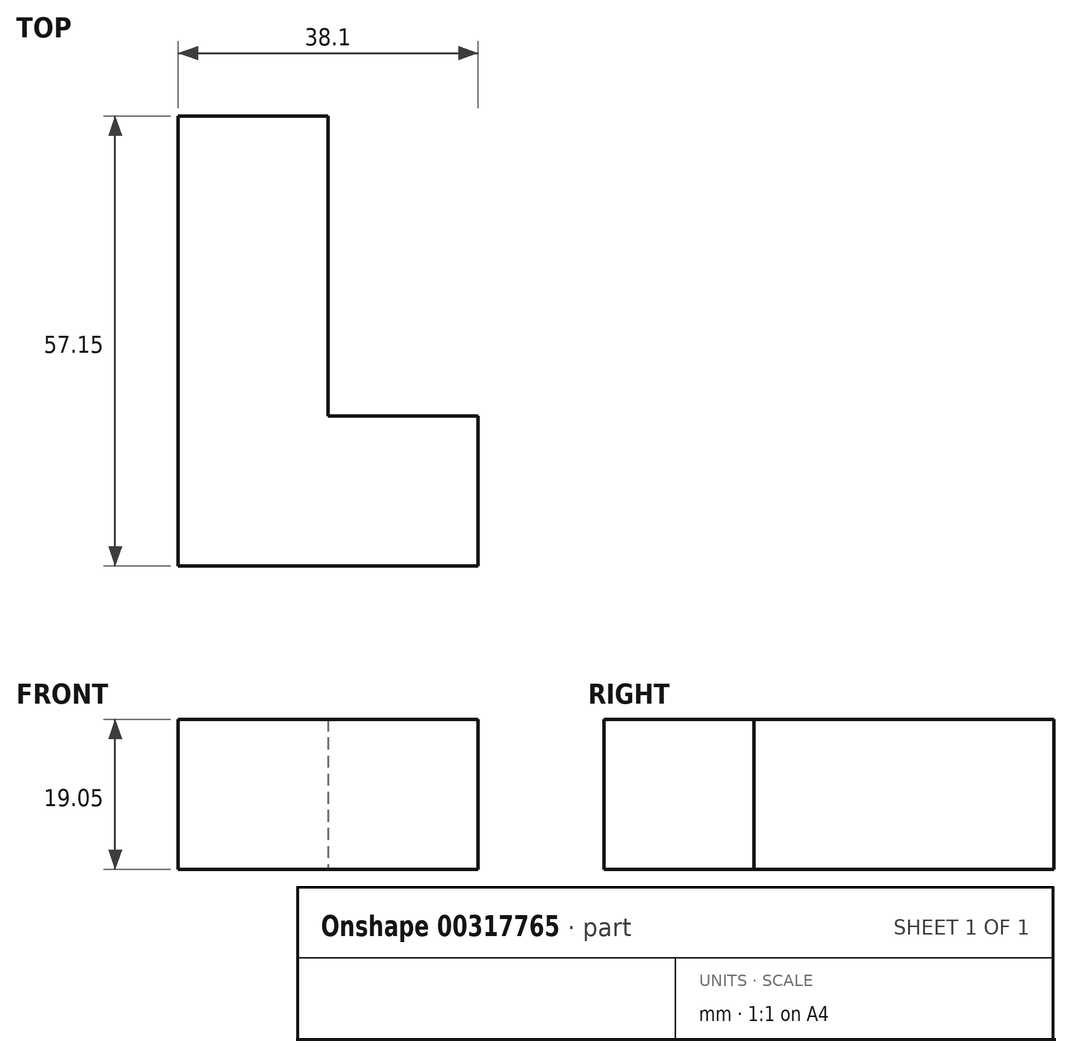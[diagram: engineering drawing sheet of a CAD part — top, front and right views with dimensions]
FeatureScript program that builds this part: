
annotation { "Feature Type Name" : "Feature", "Feature Type Description" : "" }
export const myFeature = defineFeature(function(context is Context, id is Id, definition is map)
    precondition{}
    {
        {
            var Q0;
            Q0=qCreatedBy(makeId("Top.planeOp"),FACE);
            var sketch = newSketch(context, id + "F0", { "sketchPlane" : qUnion([Q0])});
            skLineSegment(sketch, "E0.bottom", {"start": v(0, 0) * mm, "end": v(19.05, 0) * mm});
            skLineSegment(sketch, "E0.top", {"start": v(0, 57.15) * mm, "end": v(19.05, 57.15) * mm});
            skLineSegment(sketch, "E0.left", {"start": v(0, 0) * mm, "end": v(0, 57.15) * mm});
            skPoint(sketch, "E1.end.orphan", {"position": v(19.05, 28.58) * mm});
            skLineSegment(sketch, "E2", {"start": v(19.05, 57.15) * mm, "end": v(19.05, 19.05) * mm});
            skLineSegment(sketch, "E3", {"start": v(19.05, 19.05) * mm, "end": v(38.1, 19.05) * mm});
            skLineSegment(sketch, "E4", {"start": v(38.1, 19.05) * mm, "end": v(38.1, 0) * mm});
            skLineSegment(sketch, "E5", {"start": v(38.1, 0) * mm, "end": v(19.05, 0) * mm});
            skSolve(sketch);
        }
        {
            var Q0;
            Q0 = qSketchRegion(id + "F0", true);
            extrude(context, id + "F1", {"entities" : qUnion([Q0]), "depth" : 19.05 * mm});
        }
    });
